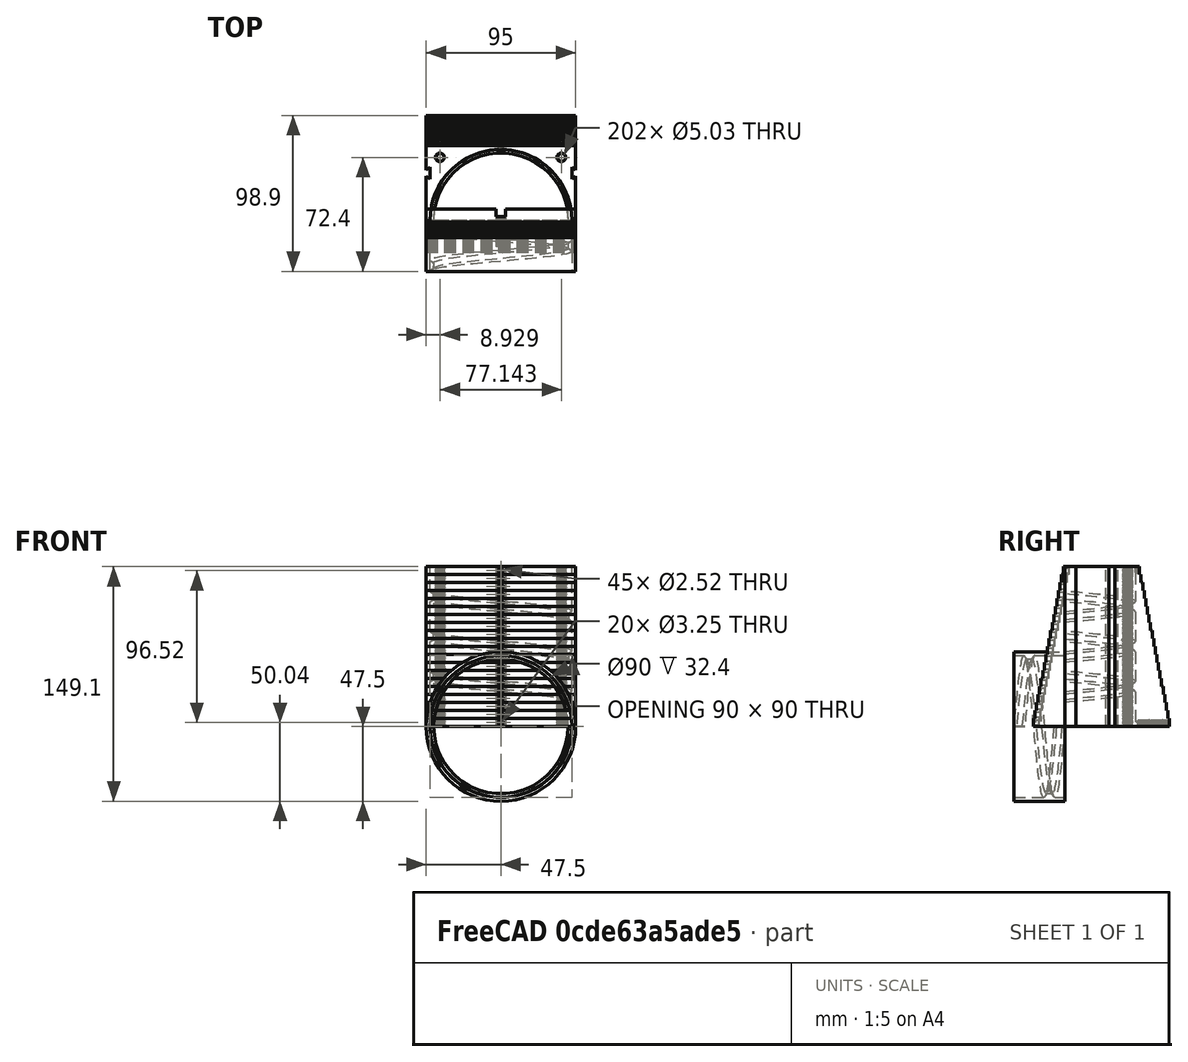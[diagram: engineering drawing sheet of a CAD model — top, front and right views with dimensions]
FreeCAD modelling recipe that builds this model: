
FCSTD DOCUMENT  (FreeCAD 2023.131R26244 +5365 (Git))
Label: Dewalt DW6184 Height Adjust
License: All rights reserved
LicenseURL: http://en.wikipedia.org/wiki/All_rights_reserved
objects: Sketcher::SketchObject×13, PartDesign::Pad×5, PartDesign::Pocket×3, PartDesign::Hole×3, PartDesign::Body×3, PartDesign::AdditiveHelix×2, Spreadsheet::Sheet×1, PartDesign::LinearPattern×1
note: 71 computed .brp shape members not serialized (recipe doc carries the construction recipe); baked Part::Feature solids carry a one-line shape summary decoded from their .brp

FEATURE [Spreadsheet::Sheet] Spreadsheet  label="Parameters"
  PythonMode = false
  ShowCells = 0
  TreeRank = 1
  cells = A1=Thickness; B1(thickness)=2.5; A2=Outer Diameter; B2(outer_diameter)=90; A3=Height; B3(height)==4"; A5=Thread Inner Width; B5(thread_small_width)=3.5; C5=4; A6=Thread Outer Width; B6(thread_large_width)=7; C6=7.5; A7=Thread Depth; B7(thread_depth)=2.3; C7=2.5; A8=Thread Turns; B8(thread_turns)=4; A9=Thread Pitch; B9(thread_pitch)==height / thread_turns; A11=Step Height Change; B11(step_height)=1; A13=Dovetail Inner Width; B13(dovetail_large_width)=7.5; A14=Dovetaile Outer Width; B14(dovetail_small_width)=4; A15=Dovetail Depth; B15(dovetail_depth)=2.5
FEATURE [Sketcher::SketchObject] Sketch
  ArcFitTolerance = 1e-06
  AttachmentSupport = -> [XY_Plane]
  ExternalBSplineMaxDegree = 5
  ExternalBSplineTolerance = 0.0001
  FullyConstrained = true
  InternalTolerance = 1e-06
  InvalidShape = false
  MakeInternals = false
  MapMode = 5
  Support = -> [XY_Plane]
  TreeRank = 12
  ValidateShape = true
  expr: Constraints[11] = <<Parameters>>.outer_diameter / 2 + <<Parameters>>.thickness - <<Parameters>>.step_height
  expr: Constraints[1] = <<Parameters>>.outer_diameter
  expr: Constraints[21] = <<Parameters>>.dovetail_small_width
  expr: Constraints[22] = <<Parameters>>.dovetail_large_width
  expr: Constraints[23] = <<Parameters>>.dovetail_depth
  expr: Constraints[26] = <<Parameters>>.outer_diameter / 3
  expr: Constraints[31] = <<Parameters>>.dovetail_large_width
  expr: Constraints[32] = <<Parameters>>.dovetail_small_width
  expr: Constraints[34] = <<Parameters>>.dovetail_depth
  expr: Constraints[36] = <<Parameters>>.outer_diameter / 3
  expr: Constraints[8] = <<Parameters>>.outer_diameter + 2 * <<Parameters>>.thickness
  sketch-geometry (16):
    g0: ArcOfCircle CenterX=0 CenterY=0 CenterZ=0 NormalX=0 NormalY=0 NormalZ=1 AngleXU=0 Radius=45 StartAngle=0 EndAngle=3.14159
    g1: LineSegment StartX=-47.5 StartY=0 StartZ=0 EndX=-45 EndY=0 EndZ=0
    g2: LineSegment StartX=47.5 StartY=0 StartZ=0 EndX=47.5 EndY=28 EndZ=0
    g3: LineSegment StartX=47.5 StartY=46.5 StartZ=0 EndX=-47.5 EndY=46.5 EndZ=0
    g4: LineSegment StartX=-47.5 StartY=46.5 StartZ=0 EndX=-47.5 EndY=32 EndZ=0
    g5: LineSegment StartX=45 StartY=0 StartZ=0 EndX=47.5 EndY=0 EndZ=0
    g6: LineSegment StartX=-47.5 StartY=32 StartZ=0 EndX=-45 EndY=33.75 EndZ=0
    g7: LineSegment StartX=-45 StartY=33.75 StartZ=0 EndX=-45 EndY=26.25 EndZ=0
    g8: LineSegment StartX=-45 StartY=26.25 StartZ=0 EndX=-47.5 EndY=28 EndZ=0
    g9: GeomPoint [constr] X=-45 Y=30 Z=0
    g10: LineSegment StartX=45 StartY=33.75 StartZ=0 EndX=45 EndY=26.25 EndZ=0
    g11: LineSegment StartX=45 StartY=26.25 StartZ=0 EndX=47.5 EndY=28 EndZ=0
    g12: LineSegment StartX=45 StartY=33.75 StartZ=0 EndX=47.5 EndY=32 EndZ=0
    g13: GeomPoint [constr] X=45 Y=30 Z=0
    g14: LineSegment StartX=-47.5 StartY=28 StartZ=0 EndX=-47.5 EndY=0 EndZ=0
    g15: LineSegment StartX=47.5 StartY=32 StartZ=0 EndX=47.5 EndY=46.5 EndZ=0
  constraints (45):
    c: Coincident(g0,g-1)
    c: Diameter(g0) = 90
    c: Coincident(g15,g3)
    c: Coincident(g3,g4)
    c: Coincident(g14,g1)
    c: Horizontal(g1)
    c: Horizontal(g3)
    c: Vertical(g4)
    c: DistanceX(g1,g5) = 95
    c: Symmetric(g1,g5,g0)
    c: Vertical(g2)
    c: DistanceY(g5,g15) = 46.5
    c: Coincident(g2,g5)
    c: Coincident(g1,g0)
    c: Coincident(g5,g0)
    c: PointOnObject(g0,g-1)
    c: PointOnObject(g0,g-1)
    c: Coincident(g7,g6)
    c: Vertical(g7)
    c: Coincident(g8,g7)
    c: Equal(g6,g8)
    c: DistanceY(g8,g6) = 4
    c: DistanceY(g7,g6) = 7.5
    c: DistanceX(g6,g6) = 2.5
    c: DistanceX(g8,g6) = 0
    c: Symmetric(g6,g7,g9)
    c: DistanceY(g0,g9) = 30
    c: Vertical(g10)
    c: Coincident(g11,g10)
    c: Coincident(g12,g10)
    c: Equal(g12,g11)
    c: DistanceY(g10,g10) = 7.5
    c: DistanceY(g11,g12) = 4
    c: DistanceX(g12,g11) = 0
    c: DistanceX(g10,g11) = 2.5
    c: Symmetric(g10,g10,g13)
    c: DistanceY(g0,g13) = 30
    c: Coincident(g4,g6)
    c: PointOnObject(g14,g8)
    c: PointOnObject(g2,g11)
    c: Coincident(g15,g12)
    c: Vertical(g14)
    c: DistanceX(g3,g1) = 0
    c: Vertical(g15)
    c: DistanceX(g3,g2) = 0
FEATURE [PartDesign::Pad] Pad
  AddSubType = 0
  AlongSketchNormal = false
  AutoTaperInnerAngle = true
  CheckUpToFaceLimits = true
  ClaimChildren = false
  Direction = (0,0,1)
  Fit = 0
  FitJoin = 0
  InnerFit = 0
  InnerFitJoin = 0
  InvalidShape = false
  Length = 101.6
  Length2 = 100
  Linearize = true
  NewSolid = false
  Profile = -> Sketch
  Suppress = false
  TaperInnerAngle = 0
  TaperInnerAngleRev = 0
  TreeRank = 13
  Type = 0
  ValidateShape = true
  _ProfileBasedVersion = 1
  expr: Length = <<Parameters>>.height
FEATURE [Sketcher::SketchObject] Sketch001
  ArcFitTolerance = 1e-06
  AttachmentSupport = -> [XZ_Plane]
  ExternalBSplineMaxDegree = 5
  ExternalBSplineTolerance = 0.0001
  FullyConstrained = true
  InternalTolerance = 1e-06
  InvalidShape = false
  MakeInternals = false
  MapMode = 5
  Placement = pos=(0,0,0) rot=(1,0,0;1.5708rad)
  Support = -> [XZ_Plane]
  TreeRank = 14
  ValidateShape = true
  expr: Constraints[10] = <<Parameters>>.outer_diameter / 2 + 0.1
  expr: Constraints[11] = <<Parameters>>.thread_large_width / 5 * 2
  expr: Constraints[7] = <<Parameters>>.thread_large_width
  expr: Constraints[8] = <<Parameters>>.thread_small_width
  expr: Constraints[9] = <<Parameters>>.thread_depth
  sketch-geometry (4):
    g0: LineSegment StartX=-45.1 StartY=9.8 StartZ=0 EndX=-45.1 EndY=2.8 EndZ=0
    g1: LineSegment StartX=-42.8 StartY=8.05 StartZ=0 EndX=-42.8 EndY=4.55 EndZ=0
    g2: LineSegment StartX=-45.1 StartY=9.8 StartZ=0 EndX=-42.8 EndY=8.05 EndZ=0
    g3: LineSegment StartX=-45.1 StartY=2.8 StartZ=0 EndX=-42.8 EndY=4.55 EndZ=0
  constraints (12):
    c: Vertical(g0)
    c: Vertical(g1)
    c: Coincident(g2,g0)
    c: Coincident(g2,g1)
    c: Coincident(g3,g0)
    c: Coincident(g3,g1)
    c: Equal(g2,g3)
    c: DistanceY(g0,g0) = 7
    c: DistanceY(g1,g1) = 3.5
    c: DistanceX(g0,g1) = 2.3
    c: DistanceX(g0,g-1) = 45.1
    c: DistanceY(g-1,g0) = 2.8
FEATURE [PartDesign::AdditiveHelix] Helix
  AddSubType = 0
  Angle = 0
  Axis = (0,-2e-16,1)
  Base = (0,0,0)
  BaseFeature = -> Pad
  ClaimChildren = false
  Fit = 0
  FitJoin = 0
  Growth = 0
  HasBeenEdited = true
  Height = 80
  InnerFit = 0
  InnerFitJoin = 0
  InvalidShape = false
  LeftHanded = false
  Linearize = true
  Mode = 0
  NewSolid = false
  Outside = false
  Pitch = 25.4
  Profile = -> Sketch001
  ReferenceAxis = -> Sketch001 [V_Axis]
  Suppress = false
  TreeRank = 15
  Turns = 3.14961
  ValidateShape = true
  _ProfileBasedVersion = 1
  expr: Pitch = <<Parameters>>.thread_pitch
  expr: Turns = <<Parameters>>.thread_turns
FEATURE [Sketcher::SketchObject] Sketch002
  ArcFitTolerance = 1e-06
  AttachmentSupport = -> [Helix]
  ExternalBSplineMaxDegree = 5
  ExternalBSplineTolerance = 0.0001
  FullyConstrained = false
  InternalTolerance = 1e-06
  InvalidShape = false
  MakeInternals = false
  MapMode = 5
  Placement = pos=(0,0,101.6) rot=(0,0,1;0rad)
  Support = -> [Helix]
  TreeRank = 16
  ValidateShape = true
  expr: Constraints[10] = <<Parameters>>.outer_diameter / 2 + 0.2
  expr: Constraints[9] = <<Parameters>>.outer_diameter + 2 * <<Parameters>>.thickness
  sketch-geometry (4):
    g0: LineSegment StartX=-47.4962 StartY=0 StartZ=0 EndX=47.5038 EndY=0 EndZ=0
    g1: LineSegment StartX=47.5038 StartY=0 StartZ=0 EndX=47.5038 EndY=-45.2 EndZ=0
    g2: LineSegment StartX=47.5038 StartY=-45.2 StartZ=0 EndX=-47.4962 EndY=-45.2 EndZ=0
    g3: LineSegment StartX=-47.4962 StartY=-45.2 StartZ=0 EndX=-47.4962 EndY=0 EndZ=0
  constraints (11):
    c: Coincident(g0,g1)
    c: Coincident(g1,g2)
    c: Coincident(g2,g3)
    c: Coincident(g3,g0)
    c: Horizontal(g0)
    c: Horizontal(g2)
    c: Vertical(g1)
    c: Vertical(g3)
    c: PointOnObject(g0,g-1)
    c: DistanceX(g0,g0) = 95
    c: DistanceY(g1,g0) = 45.2
FEATURE [PartDesign::Pocket] Pocket
  AddSubType = 1
  AutoTaperInnerAngle = true
  BaseFeature = -> Helix
  CheckUpToFaceLimits = true
  ClaimChildren = false
  Fit = 0
  FitJoin = 0
  InnerFit = 0
  InnerFitJoin = 0
  InvalidShape = false
  Length = 500
  Length2 = 500
  Linearize = true
  NewSolid = false
  Profile = -> Sketch002
  Suppress = false
  TaperInnerAngle = 0
  TaperInnerAngleRev = 0
  TreeRank = 17
  Type = 4
  ValidateShape = true
  _ProfileBasedVersion = 1
  _Version = 1
FEATURE [Sketcher::SketchObject] Sketch003
  ArcFitTolerance = 1e-06
  AttachmentSupport = -> [Pocket]
  ExternalBSplineMaxDegree = 5
  ExternalBSplineTolerance = 0.0001
  FullyConstrained = true
  InternalTolerance = 1e-06
  InvalidShape = false
  MakeInternals = false
  MapMode = 5
  Placement = pos=(-47.5,0,0) rot=(0.57735,-0.57735,-0.57735;2.0944rad)
  Support = -> [Pocket]
  TreeRank = 18
  ValidateShape = true
  expr: Constraints[2] = <<Parameters>>.outer_diameter / 2 + <<Parameters>>.thickness - <<Parameters>>.step_height
  expr: Constraints[3] = <<Parameters>>.height
  expr: Constraints[7] = <<Parameters>>.step_height
  sketch-geometry (42):
    g0: LineSegment StartX=-46.5 StartY=101.6 StartZ=0 EndX=-46.5 EndY=0 EndZ=0
    g1: LineSegment StartX=-47.5 StartY=101.6 StartZ=0 EndX=-47.5 EndY=96.52 EndZ=0
    g2: LineSegment StartX=-48.5 StartY=96.52 StartZ=0 EndX=-48.5 EndY=91.44 EndZ=0
    g3: LineSegment StartX=-47.5 StartY=96.52 StartZ=0 EndX=-48.5 EndY=96.52 EndZ=0
    g4: LineSegment StartX=-48.5 StartY=91.44 StartZ=0 EndX=-49.5 EndY=91.44 EndZ=0
    g5: LineSegment StartX=-49.5 StartY=91.44 StartZ=0 EndX=-49.5 EndY=86.36 EndZ=0
    g6: LineSegment StartX=-49.5 StartY=86.36 StartZ=0 EndX=-50.5 EndY=86.36 EndZ=0
    g7: LineSegment StartX=-50.5 StartY=86.36 StartZ=0 EndX=-50.5 EndY=81.28 EndZ=0
    g8: LineSegment StartX=-50.5 StartY=81.28 StartZ=0 EndX=-51.5 EndY=81.28 EndZ=0
    g9: LineSegment StartX=-51.5 StartY=81.28 StartZ=0 EndX=-51.5 EndY=76.2 EndZ=0
    g10: LineSegment StartX=-51.5 StartY=76.2 StartZ=0 EndX=-52.5 EndY=76.2 EndZ=0
    g11: LineSegment StartX=-52.5 StartY=76.2 StartZ=0 EndX=-52.5 EndY=71.12 EndZ=0
    g12: LineSegment StartX=-47.5 StartY=101.6 StartZ=0 EndX=-46.5 EndY=101.6 EndZ=0
    g13: LineSegment StartX=-52.5 StartY=71.12 StartZ=0 EndX=-53.5 EndY=71.12 EndZ=0
    g14: LineSegment StartX=-53.5 StartY=71.12 StartZ=0 EndX=-53.5 EndY=66.04 EndZ=0
    g15: LineSegment StartX=-53.5 StartY=66.04 StartZ=0 EndX=-54.5 EndY=66.04 EndZ=0
    g16: LineSegment StartX=-54.5 StartY=66.04 StartZ=0 EndX=-54.5 EndY=60.96 EndZ=0
    g17: LineSegment StartX=-54.5 StartY=60.96 StartZ=0 EndX=-55.5 EndY=60.96 EndZ=0
    g18: LineSegment StartX=-55.5 StartY=60.96 StartZ=0 EndX=-55.5 EndY=55.88 EndZ=0
    g19: LineSegment StartX=-55.5 StartY=55.88 StartZ=0 EndX=-56.5 EndY=55.88 EndZ=0
    g20: LineSegment StartX=-56.5 StartY=55.88 StartZ=0 EndX=-56.5 EndY=50.8 EndZ=0
    g21: LineSegment StartX=-56.5 StartY=50.8 StartZ=0 EndX=-57.5 EndY=50.8 EndZ=0
    g22: LineSegment StartX=-57.5 StartY=50.8 StartZ=0 EndX=-57.5 EndY=45.72 EndZ=0
    g23: LineSegment StartX=-57.5 StartY=45.72 StartZ=0 EndX=-58.5 EndY=45.72 EndZ=0
    g24: LineSegment StartX=-58.5 StartY=45.72 StartZ=0 EndX=-58.5 EndY=40.64 EndZ=0
    g25: LineSegment StartX=-58.5 StartY=40.64 StartZ=0 EndX=-59.5 EndY=40.64 EndZ=0
    g26: LineSegment StartX=-59.5 StartY=40.64 StartZ=0 EndX=-59.5 EndY=35.56 EndZ=0
    g27: LineSegment StartX=-59.5 StartY=35.56 StartZ=0 EndX=-60.5 EndY=35.56 EndZ=0
    g28: LineSegment StartX=-60.5 StartY=35.56 StartZ=0 EndX=-60.5 EndY=30.48 EndZ=0
    g29: LineSegment StartX=-60.5 StartY=30.48 StartZ=0 EndX=-61.5 EndY=30.48 EndZ=0
    g30: LineSegment StartX=-61.5 StartY=30.48 StartZ=0 EndX=-61.5 EndY=25.4 EndZ=0
    g31: LineSegment StartX=-61.5 StartY=25.4 StartZ=0 EndX=-62.5 EndY=25.4 EndZ=0
    g32: LineSegment StartX=-62.5 StartY=25.4 StartZ=0 EndX=-62.5 EndY=20.32 EndZ=0
    g33: LineSegment StartX=-62.5 StartY=20.32 StartZ=0 EndX=-63.5 EndY=20.32 EndZ=0
    g34: LineSegment StartX=-63.5 StartY=20.32 StartZ=0 EndX=-63.5 EndY=15.24 EndZ=0
    g35: LineSegment StartX=-63.5 StartY=15.24 StartZ=0 EndX=-64.5 EndY=15.24 EndZ=0
    g36: LineSegment StartX=-64.5 StartY=15.24 StartZ=0 EndX=-64.5 EndY=10.16 EndZ=0
    g37: LineSegment StartX=-64.5 StartY=10.16 StartZ=0 EndX=-65.5 EndY=10.16 EndZ=0
    g38: LineSegment StartX=-65.5 StartY=10.16 StartZ=0 EndX=-65.5 EndY=5.08 EndZ=0
    g39: LineSegment StartX=-65.5 StartY=5.08 StartZ=0 EndX=-66.5 EndY=5.08 EndZ=0
    g40: LineSegment StartX=-66.5 StartY=5.08 StartZ=0 EndX=-66.5 EndY=0 EndZ=0
    g41: LineSegment StartX=-66.5 StartY=0 StartZ=0 EndX=-46.5 EndY=0 EndZ=0
  constraints (126):
    c: PointOnObject(g0,g-1)
    c: Vertical(g0)
    c: DistanceX(g0,g-1) = 46.5
    c: DistanceY(g0,g0) = 101.6
    c: Vertical(g1)
    c: Vertical(g2)
    c: Equal(g1,g2)
    c: DistanceX(g2,g1) = 1
    c: Coincident(g3,g1)
    c: Horizontal(g3)
    c: Coincident(g2,g3)
    c: Coincident(g4,g2)
    c: Horizontal(g4)
    c: Coincident(g5,g4)
    c: Vertical(g5)
    c: Equal(g3,g4)
    c: Coincident(g6,g5)
    c: Horizontal(g6)
    c: Coincident(g7,g6)
    c: Vertical(g7)
    c: Coincident(g8,g7)
    c: Horizontal(g8)
    c: Coincident(g9,g8)
    c: Vertical(g9)
    c: Coincident(g10,g9)
    c: Horizontal(g10)
    c: Coincident(g11,g10)
    c: Vertical(g11)
    c: Equal(g3,g6)
    c: Equal(g3,g8)
    c: Equal(g3,g10)
    c: Equal(g1,g5)
    c: Equal(g1,g7)
    c: Equal(g1,g9)
    c: Equal(g1,g11)
    c: Coincident(g12,g1)
    c: Horizontal(g12)
    c: Equal(g3,g12)
    c: Coincident(g12,g0)
    c: Coincident(g13,g11)
    c: Horizontal(g13)
    c: Coincident(g14,g13)
    c: Vertical(g14)
    c: Coincident(g15,g14)
    c: Horizontal(g15)
    c: Coincident(g16,g15)
    c: Vertical(g16)
    c: Coincident(g17,g16)
    c: Horizontal(g17)
    c: Coincident(g18,g17)
    c: Vertical(g18)
    c: Coincident(g19,g18)
    c: Horizontal(g19)
    c: Coincident(g20,g19)
    c: Vertical(g20)
    c: Coincident(g21,g20)
    c: Horizontal(g21)
    c: Coincident(g22,g21)
    c: Vertical(g22)
    c: Coincident(g23,g22)
    c: Horizontal(g23)
    c: Coincident(g24,g23)
    c: Vertical(g24)
    c: Coincident(g25,g24)
    c: Horizontal(g25)
    c: Coincident(g26,g25)
    c: Vertical(g26)
    c: Coincident(g27,g26)
    c: Horizontal(g27)
    c: Coincident(g28,g27)
    c: Vertical(g28)
    c: Coincident(g29,g28)
    c: Horizontal(g29)
    c: Coincident(g30,g29)
    c: Vertical(g30)
    c: Coincident(g31,g30)
    c: Horizontal(g31)
    c: Coincident(g32,g31)
    c: Vertical(g32)
    c: Coincident(g33,g32)
    c: Horizontal(g33)
    c: Coincident(g34,g33)
    c: Vertical(g34)
    c: Coincident(g35,g34)
    c: Horizontal(g35)
    c: Coincident(g36,g35)
    c: Vertical(g36)
    c: Coincident(g37,g36)
    c: Horizontal(g37)
    c: Coincident(g38,g37)
    c: Vertical(g38)
    c: Coincident(g39,g38)
    c: Horizontal(g39)
    c: Coincident(g40,g39)
    c: Vertical(g40)
    c: Equal(g13,g10)
    c: Equal(g13,g15)
    c: Equal(g15,g17)
    c: Equal(g17,g19)
    c: Equal(g19,g21)
    c: Equal(g21,g23)
    c: Equal(g23,g25)
    c: Equal(g25,g27)
    c: Equal(g27,g29)
    c: Equal(g29,g31)
    c: Equal(g31,g33)
    c: Equal(g33,g35)
    c: Equal(g35,g37)
    c: Equal(g37,g39)
    c: Equal(g11,g14)
    c: Equal(g14,g16)
    c: Equal(g16,g18)
    c: Equal(g18,g20)
    c: Equal(g20,g22)
    c: Equal(g22,g24)
    c: Equal(g24,g26)
    c: Equal(g26,g28)
    c: Equal(g28,g30)
    c: Equal(g30,g32)
    c: Equal(g32,g34)
    c: Equal(g34,g36)
    c: Equal(g36,g38)
    c: Equal(g38,g40)
    c: PointOnObject(g40,g-1)
    c: Coincident(g41,g40)
    c: Coincident(g41,g0)
FEATURE [PartDesign::Pad] Pad001
  AddSubType = 0
  AlongSketchNormal = false
  AutoTaperInnerAngle = true
  BaseFeature = -> Pocket
  CheckUpToFaceLimits = true
  ClaimChildren = false
  Direction = (-1,0,0)
  Fit = 0
  FitJoin = 0
  InnerFit = 0
  InnerFitJoin = 0
  InvalidShape = false
  Length = 95
  Length2 = 100
  Linearize = true
  NewSolid = false
  Profile = -> Sketch003
  Reversed = true
  Suppress = false
  TaperInnerAngle = 0
  TaperInnerAngleRev = 0
  TreeRank = 19
  Type = 0
  ValidateShape = true
  _ProfileBasedVersion = 1
  expr: Length = <<Parameters>>.outer_diameter + 2 * <<Parameters>>.thickness
FEATURE [Sketcher::SketchObject] Sketch004
  ArcFitTolerance = 1e-06
  AttachmentSupport = -> [Pad001]
  ExternalBSplineMaxDegree = 5
  ExternalBSplineTolerance = 0.0001
  FullyConstrained = true
  InternalTolerance = 1e-06
  InvalidShape = false
  MakeInternals = false
  MapMode = 5
  Placement = pos=(0,0,101.6) rot=(0,0,1;0rad)
  Support = -> [Pad001]
  TreeRank = 20
  ValidateShape = true
  expr: Constraints[1] = <<Parameters>>.outer_diameter / 9 * 4
  expr: Constraints[2] = <<Parameters>>.outer_diameter / 7 * 6
  sketch-geometry (2):
    g0: Circle CenterX=-38.5714 CenterY=40 CenterZ=0 NormalX=0 NormalY=0 NormalZ=1 AngleXU=0 Radius=3
    g1: Circle CenterX=38.5714 CenterY=40 CenterZ=0 NormalX=0 NormalY=0 NormalZ=1 AngleXU=0 Radius=3
  constraints (5):
    c: Symmetric(g0,g1,g-2)
    c: DistanceY(g-1,g0) = 40
    c: DistanceX(g0,g1) = 77.1429
    c: Equal(g0,g1)
    c: Diameter(g0) = 6
FEATURE [PartDesign::Hole] Hole
  AddSubType = 1
  BaseFeature = -> Pad001
  ClaimChildren = false
  CustomThreadClearance = 0
  Depth = 101.6
  DepthType = 0
  Diameter = 5.026
  DrillForDepth = false
  DrillPoint = 0
  DrillPointAngle = 118
  Fit = 0
  FitJoin = 0
  HoleCutCountersinkAngle = 90
  HoleCutCustomValues = false
  HoleCutDepth = 0
  HoleCutDiameter = 6.1
  HoleCutType = 0
  InnerFit = 0
  InnerFitJoin = 0
  InvalidShape = false
  Linearize = true
  ModelThread = true
  NewSolid = false
  Profile = -> Sketch004
  Suppress = false
  Tapered = false
  TaperedAngle = 90
  ThreadClass = 0
  ThreadDepth = 101.6
  ThreadDepthType = 0
  ThreadDirection = 0
  ThreadFit = 0
  ThreadSize = 14
  ThreadType = 1
  Threaded = true
  TreeRank = 21
  UseCustomThreadClearance = false
  ValidateShape = true
  _ProfileBasedVersion = 1
  expr: Depth = <<Parameters>>.height
FEATURE [Sketcher::SketchObject] Sketch005
  ArcFitTolerance = 1e-06
  AttachmentSupport = -> [Hole]
  ExternalBSplineMaxDegree = 5
  ExternalBSplineTolerance = 0.0001
  FullyConstrained = true
  InternalTolerance = 1e-06
  InvalidShape = false
  MakeInternals = false
  MapMode = 5
  Placement = pos=(0,66.5,0) rot=(0,0.707107,0.707107;3.14159rad)
  Support = -> [Hole]
  TreeRank = 22
  ValidateShape = true
  expr: Constraints[2] = <<Parameters>>.height / 20 / 2
  sketch-geometry (1):
    g0: Circle CenterX=0 CenterY=2.54 CenterZ=0 NormalX=0 NormalY=0 NormalZ=1 AngleXU=0 Radius=1.5
  constraints (3):
    c: PointOnObject(g0,g-2)
    c: Diameter(g0) = 3
    c: DistanceY(g-1,g0) = 2.54
FEATURE [PartDesign::Hole] Hole001
  AddSubType = 1
  BaseFeature = -> Hole
  ClaimChildren = false
  CustomThreadClearance = 0
  Depth = 20
  DepthType = 0
  Diameter = 2.52
  DrillForDepth = false
  DrillPoint = 1
  DrillPointAngle = 118
  Fit = 0
  FitJoin = 0
  HoleCutCountersinkAngle = 90
  HoleCutCustomValues = false
  HoleCutDepth = 0
  HoleCutDiameter = 6.1
  HoleCutType = 0
  InnerFit = 0
  InnerFitJoin = 0
  InvalidShape = false
  Linearize = true
  ModelThread = true
  NewSolid = false
  Profile = -> Sketch005
  Suppress = false
  Tapered = false
  TaperedAngle = 90
  ThreadClass = 0
  ThreadDepth = 20
  ThreadDepthType = 0
  ThreadDirection = 0
  ThreadFit = 0
  ThreadSize = 9
  ThreadType = 1
  Threaded = true
  TreeRank = 23
  UseCustomThreadClearance = false
  ValidateShape = true
  _ProfileBasedVersion = 1
  expr: Depth = 20
FEATURE [Sketcher::SketchObject] Sketch006
  ArcFitTolerance = 1e-06
  AttachmentSupport = -> [Hole001]
  ExternalBSplineMaxDegree = 5
  ExternalBSplineTolerance = 0.0001
  FullyConstrained = false
  InternalTolerance = 1e-06
  InvalidShape = false
  MakeInternals = false
  MapMode = 5
  Placement = pos=(0,47.5,0) rot=(0,0.707107,0.707107;3.14159rad)
  Support = -> [Hole001]
  TreeRank = 24
  ValidateShape = true
  expr: Constraints[1] = <<Parameters>>.height / 40 * 39
  sketch-geometry (1):
    g0: Circle CenterX=0 CenterY=99.06 CenterZ=0 NormalX=0 NormalY=0 NormalZ=1 AngleXU=0 Radius=2.09662
  constraints (2):
    c: PointOnObject(g0,g-2)
    c: DistanceY(g-1,g0) = 99.06
FEATURE [PartDesign::Hole] Hole002
  AddSubType = 1
  BaseFeature = -> Hole001
  ClaimChildren = false
  CustomThreadClearance = 0
  Depth = 5
  DepthType = 0
  Diameter = 2.52
  DrillForDepth = false
  DrillPoint = 1
  DrillPointAngle = 118
  Fit = 0
  FitJoin = 0
  HoleCutCountersinkAngle = 90
  HoleCutCustomValues = false
  HoleCutDepth = 0
  HoleCutDiameter = 6.1
  HoleCutType = 0
  InnerFit = 0
  InnerFitJoin = 0
  InvalidShape = false
  Linearize = true
  ModelThread = true
  NewSolid = false
  Profile = -> Sketch006
  Suppress = false
  Tapered = false
  TaperedAngle = 90
  ThreadClass = 0
  ThreadDepth = 5
  ThreadDepthType = 0
  ThreadDirection = 0
  ThreadFit = 0
  ThreadSize = 9
  ThreadType = 1
  Threaded = true
  TreeRank = 25
  UseCustomThreadClearance = false
  ValidateShape = true
  _ProfileBasedVersion = 1
FEATURE [PartDesign::Body] Body  label="Cradle"
  AutoGroupSolids = false
  ClaimAllChildren = false
  ExportMode = 0
  Group = -> [Sketch,Pad,Sketch001,Helix,Sketch002,Pocket,Sketch003,Pad001,Sketch004,Hole,Sketch005,Hole001,Sketch006,Hole002]
  InvalidShape = false
  Origin = -> Origin
  Tip = -> Hole002
  TreeRank = 11
  ValidateShape = true
  _ExportChildren = -> [Pad,Helix,Pocket,Pad001,Hole,Hole001,Hole002]
  _GroupVersion = 1
FEATURE [Sketcher::SketchObject] Sketch007
  ArcFitTolerance = 1e-06
  AttachmentOffset = pos=(0,0,-47.5) rot=(0,0,1;0rad)
  AttachmentSupport = -> [YZ_Plane001]
  ExternalBSplineMaxDegree = 5
  ExternalBSplineTolerance = 0.0001
  FullyConstrained = true
  InternalTolerance = 1e-06
  InvalidShape = false
  MakeInternals = false
  MapMode = 5
  Placement = pos=(-47.5,1.05e-14,-1.05e-14) rot=(0.57735,0.57735,0.57735;2.0944rad)
  Support = -> [YZ_Plane001]
  TreeRank = 36
  ValidateShape = true
  expr: AttachmentOffset.Base.z = -<<Parameters>>.outer_diameter / 2 - <<Parameters>>.thickness
  expr: Constraints[124] = <<Parameters>>.step_height
  expr: Constraints[2] = <<Parameters>>.height
  sketch-geometry (42):
    g0: LineSegment StartX=0 StartY=0 StartZ=0 EndX=0 EndY=101.6 EndZ=0
    g1: LineSegment StartX=0 StartY=101.6 StartZ=0 EndX=-1 EndY=101.6 EndZ=0
    g2: LineSegment StartX=-1 StartY=101.6 StartZ=0 EndX=-1 EndY=96.52 EndZ=0
    g3: LineSegment StartX=-1 StartY=96.52 StartZ=0 EndX=-2 EndY=96.52 EndZ=0
    g4: LineSegment StartX=-2 StartY=96.52 StartZ=0 EndX=-2 EndY=91.44 EndZ=0
    g5: LineSegment StartX=-2 StartY=91.44 StartZ=0 EndX=-3 EndY=91.44 EndZ=0
    g6: LineSegment StartX=-3 StartY=91.44 StartZ=0 EndX=-3 EndY=86.36 EndZ=0
    g7: LineSegment StartX=-3 StartY=86.36 StartZ=0 EndX=-4 EndY=86.36 EndZ=0
    g8: LineSegment StartX=-4 StartY=86.36 StartZ=0 EndX=-4 EndY=81.28 EndZ=0
    g9: LineSegment StartX=-4 StartY=81.28 StartZ=0 EndX=-5 EndY=81.28 EndZ=0
    g10: LineSegment StartX=-5 StartY=81.28 StartZ=0 EndX=-5 EndY=76.2 EndZ=0
    g11: LineSegment StartX=-5 StartY=76.2 StartZ=0 EndX=-6 EndY=76.2 EndZ=0
    g12: LineSegment StartX=-6 StartY=76.2 StartZ=0 EndX=-6 EndY=71.12 EndZ=0
    g13: LineSegment StartX=-6 StartY=71.12 StartZ=0 EndX=-7 EndY=71.12 EndZ=0
    g14: LineSegment StartX=-7 StartY=71.12 StartZ=0 EndX=-7 EndY=66.04 EndZ=0
    g15: LineSegment StartX=-7 StartY=66.04 StartZ=0 EndX=-8 EndY=66.04 EndZ=0
    g16: LineSegment StartX=-8 StartY=66.04 StartZ=0 EndX=-8 EndY=60.96 EndZ=0
    g17: LineSegment StartX=-8 StartY=60.96 StartZ=0 EndX=-9 EndY=60.96 EndZ=0
    g18: LineSegment StartX=-9 StartY=60.96 StartZ=0 EndX=-9 EndY=55.88 EndZ=0
    g19: LineSegment StartX=-9 StartY=55.88 StartZ=0 EndX=-10 EndY=55.88 EndZ=0
    g20: LineSegment StartX=-10 StartY=55.88 StartZ=0 EndX=-10 EndY=50.8 EndZ=0
    g21: LineSegment StartX=-10 StartY=50.8 StartZ=0 EndX=-11 EndY=50.8 EndZ=0
    g22: LineSegment StartX=-11 StartY=50.8 StartZ=0 EndX=-11 EndY=45.72 EndZ=0
    g23: LineSegment StartX=-11 StartY=45.72 StartZ=0 EndX=-12 EndY=45.72 EndZ=0
    g24: LineSegment StartX=-12 StartY=45.72 StartZ=0 EndX=-12 EndY=40.64 EndZ=0
    g25: LineSegment StartX=-12 StartY=40.64 StartZ=0 EndX=-13 EndY=40.64 EndZ=0
    g26: LineSegment StartX=-13 StartY=40.64 StartZ=0 EndX=-13 EndY=35.56 EndZ=0
    g27: LineSegment StartX=-13 StartY=35.56 StartZ=0 EndX=-14 EndY=35.56 EndZ=0
    g28: LineSegment StartX=-14 StartY=35.56 StartZ=0 EndX=-14 EndY=30.48 EndZ=0
    g29: LineSegment StartX=-14 StartY=30.48 StartZ=0 EndX=-15 EndY=30.48 EndZ=0
    g30: LineSegment StartX=-15 StartY=30.48 StartZ=0 EndX=-15 EndY=25.4 EndZ=0
    g31: LineSegment StartX=-15 StartY=25.4 StartZ=0 EndX=-16 EndY=25.4 EndZ=0
    g32: LineSegment StartX=-16 StartY=25.4 StartZ=0 EndX=-16 EndY=20.32 EndZ=0
    g33: LineSegment StartX=-16 StartY=20.32 StartZ=0 EndX=-17 EndY=20.32 EndZ=0
    g34: LineSegment StartX=-17 StartY=20.32 StartZ=0 EndX=-17 EndY=15.24 EndZ=0
    g35: LineSegment StartX=-17 StartY=15.24 StartZ=0 EndX=-18 EndY=15.24 EndZ=0
    g36: LineSegment StartX=-18 StartY=15.24 StartZ=0 EndX=-18 EndY=10.16 EndZ=0
    g37: LineSegment StartX=-18 StartY=10.16 StartZ=0 EndX=-19 EndY=10.16 EndZ=0
    g38: LineSegment StartX=-19 StartY=10.16 StartZ=0 EndX=-19 EndY=5.08 EndZ=0
    g39: LineSegment StartX=-19 StartY=5.08 StartZ=0 EndX=-20 EndY=5.08 EndZ=0
    g40: LineSegment StartX=-20 StartY=5.08 StartZ=0 EndX=-20 EndY=0 EndZ=0
    g41: LineSegment StartX=-20 StartY=0 StartZ=0 EndX=0 EndY=0 EndZ=0
  constraints (125):
    c: Coincident(g0,g-1)
    c: PointOnObject(g0,g-2)
    c: DistanceY(g0,g0) = 101.6
    c: Coincident(g1,g0)
    c: Horizontal(g1)
    c: Coincident(g2,g1)
    c: Vertical(g2)
    c: Coincident(g3,g2)
    c: Horizontal(g3)
    c: Coincident(g4,g3)
    c: Vertical(g4)
    c: Coincident(g5,g4)
    c: Horizontal(g5)
    c: Coincident(g6,g5)
    c: Vertical(g6)
    c: Coincident(g7,g6)
    c: Horizontal(g7)
    c: Coincident(g8,g7)
    c: Vertical(g8)
    c: Coincident(g9,g8)
    c: Horizontal(g9)
    c: Coincident(g10,g9)
    c: Vertical(g10)
    c: Coincident(g11,g10)
    c: Coincident(g12,g11)
    c: Vertical(g12)
    c: Coincident(g13,g12)
    c: Coincident(g14,g13)
    c: Vertical(g14)
    c: Horizontal(g11)
    c: Horizontal(g13)
    c: Equal(g1,g3)
    c: Equal(g3,g5)
    c: Equal(g5,g7)
    c: Equal(g7,g9)
    c: Equal(g9,g11)
    c: Equal(g11,g13)
    c: Equal(g2,g4)
    c: Equal(g4,g6)
    c: Equal(g6,g8)
    c: Equal(g8,g10)
    c: Equal(g10,g12)
    c: Equal(g12,g14)
    c: Coincident(g15,g14)
    c: Horizontal(g15)
    c: Coincident(g16,g15)
    c: Vertical(g16)
    c: Coincident(g17,g16)
    c: Horizontal(g17)
    c: Coincident(g18,g17)
    c: Vertical(g18)
    c: Coincident(g19,g18)
    c: Horizontal(g19)
    c: Coincident(g20,g19)
    c: Vertical(g20)
    c: Coincident(g21,g20)
    c: Horizontal(g21)
    c: Coincident(g22,g21)
    c: Vertical(g22)
    c: Coincident(g23,g22)
    c: Horizontal(g23)
    c: Coincident(g24,g23)
    c: Vertical(g24)
    c: Coincident(g25,g24)
    c: Horizontal(g25)
    c: Coincident(g26,g25)
    c: Vertical(g26)
    c: Coincident(g27,g26)
    c: Horizontal(g27)
    c: Coincident(g28,g27)
    c: Vertical(g28)
    c: Coincident(g29,g28)
    c: Horizontal(g29)
    c: Coincident(g30,g29)
    c: Vertical(g30)
    c: Coincident(g31,g30)
    c: Horizontal(g31)
    c: Coincident(g32,g31)
    c: Vertical(g32)
    c: Coincident(g33,g32)
    c: Horizontal(g33)
    c: Coincident(g34,g33)
    c: Vertical(g34)
    c: Coincident(g35,g34)
    c: Horizontal(g35)
    c: Coincident(g36,g35)
    c: Vertical(g36)
    c: Coincident(g37,g36)
    c: Horizontal(g37)
    c: Coincident(g38,g37)
    c: Vertical(g38)
    c: Coincident(g39,g38)
    c: Horizontal(g39)
    c: Coincident(g40,g39)
    c: Vertical(g40)
    c: Coincident(g41,g40)
    c: Horizontal(g41)
    c: Equal(g13,g15)
    c: Equal(g15,g17)
    c: Equal(g17,g19)
    c: Equal(g19,g21)
    c: Equal(g21,g23)
    c: Equal(g23,g25)
    c: Equal(g25,g27)
    c: Equal(g27,g29)
    c: Equal(g29,g31)
    c: Equal(g31,g33)
    c: Equal(g33,g35)
    c: Equal(g35,g37)
    c: Equal(g37,g39)
    c: Equal(g14,g16)
    c: Equal(g16,g18)
    c: Equal(g18,g20)
    c: Equal(g20,g22)
    c: Equal(g22,g24)
    c: Equal(g24,g26)
    c: Equal(g26,g28)
    c: Equal(g28,g30)
    c: Equal(g30,g32)
    c: Equal(g32,g34)
    c: Equal(g34,g36)
    c: Equal(g36,g38)
    c: Equal(g38,g40)
    c: Coincident(g41,g0)
    c: DistanceX(g3,g2) = 1
FEATURE [PartDesign::Pad] Pad002
  AddSubType = 0
  AlongSketchNormal = false
  AutoTaperInnerAngle = true
  CheckUpToFaceLimits = true
  ClaimChildren = false
  Direction = (1,-2e-16,3e-16)
  Fit = 0
  FitJoin = 0
  InnerFit = 0
  InnerFitJoin = 0
  InvalidShape = false
  Length = 95
  Length2 = 100
  Linearize = true
  NewSolid = false
  Profile = -> Sketch007
  Suppress = false
  TaperInnerAngle = 0
  TaperInnerAngleRev = 0
  TreeRank = 37
  Type = 0
  ValidateShape = true
  _ProfileBasedVersion = 1
  expr: Length = <<Parameters>>.outer_diameter + 2 * <<Parameters>>.thickness
FEATURE [Sketcher::SketchObject] Sketch008
  ArcFitTolerance = 1e-06
  AttachmentSupport = -> [Pad002]
  ExternalBSplineMaxDegree = 5
  ExternalBSplineTolerance = 0.0001
  FullyConstrained = true
  InternalTolerance = 1e-06
  InvalidShape = false
  MakeInternals = false
  MapMode = 5
  Placement = pos=(0,0,0) rot=(0,0.707107,0.707107;3.14159rad)
  Support = -> [Pad002]
  TreeRank = 38
  ValidateShape = true
  expr: Constraints[10] = <<Parameters>>.height
  expr: Constraints[9] = <<Parameters>>.outer_diameter + 2 * <<Parameters>>.thickness
  sketch-geometry (4):
    g0: LineSegment StartX=-47.5 StartY=0 StartZ=0 EndX=47.5 EndY=0 EndZ=0
    g1: LineSegment StartX=47.5 StartY=0 StartZ=0 EndX=47.5 EndY=101.6 EndZ=0
    g2: LineSegment StartX=47.5 StartY=101.6 StartZ=0 EndX=-47.5 EndY=101.6 EndZ=0
    g3: LineSegment StartX=-47.5 StartY=101.6 StartZ=0 EndX=-47.5 EndY=0 EndZ=0
  constraints (11):
    c: Coincident(g0,g1)
    c: Coincident(g1,g2)
    c: Coincident(g2,g3)
    c: Coincident(g3,g0)
    c: Horizontal(g0)
    c: Horizontal(g2)
    c: Vertical(g1)
    c: Vertical(g3)
    c: Symmetric(g0,g0,g-1)
    c: DistanceX(g0,g0) = 95
    c: DistanceY(g0,g1) = 101.6
FEATURE [PartDesign::Pad] Pad003
  AddSubType = 0
  AlongSketchNormal = false
  AutoTaperInnerAngle = true
  BaseFeature = -> Pad002
  CheckUpToFaceLimits = true
  ClaimChildren = false
  Direction = (2e-16,1,-2e-16)
  Fit = 0
  FitJoin = 0
  InnerFit = 0
  InnerFitJoin = 0
  InvalidShape = false
  Length = 7
  Length2 = 100
  Linearize = true
  NewSolid = false
  Profile = -> Sketch008
  Suppress = false
  TaperInnerAngle = 0
  TaperInnerAngleRev = 0
  TreeRank = 39
  Type = 0
  ValidateShape = true
  _ProfileBasedVersion = 1
  expr: Length = <<Parameters>>.thickness + 4.5
FEATURE [Sketcher::SketchObject] Sketch009
  ArcFitTolerance = 1e-06
  AttachmentSupport = -> [YZ_Plane001]
  ExternalBSplineMaxDegree = 5
  ExternalBSplineTolerance = 0.0001
  FullyConstrained = true
  InternalTolerance = 1e-06
  InvalidShape = false
  MakeInternals = false
  MapMode = 5
  Placement = pos=(0,0,0) rot=(0.57735,0.57735,0.57735;2.0944rad)
  Support = -> [YZ_Plane001]
  TreeRank = 40
  ValidateShape = true
  expr: Constraints[124] = <<Parameters>>.thickness + 4.5
  expr: Constraints[125] = <<Parameters>>.thickness
  expr: Constraints[3] = <<Parameters>>.step_height
  expr: Constraints[40] = <<Parameters>>.height
  sketch-geometry (42):
    g0: LineSegment StartX=2.5 StartY=101.6 StartZ=0 EndX=2.5 EndY=96.52 EndZ=0
    g1: LineSegment StartX=2.5 StartY=96.52 StartZ=0 EndX=1.5 EndY=96.52 EndZ=0
    g2: LineSegment StartX=1.5 StartY=96.52 StartZ=0 EndX=1.5 EndY=91.44 EndZ=0
    g3: LineSegment StartX=1.5 StartY=91.44 StartZ=0 EndX=0.5 EndY=91.44 EndZ=0
    g4: LineSegment StartX=0.5 StartY=91.44 StartZ=0 EndX=0.5 EndY=86.36 EndZ=0
    g5: LineSegment StartX=0.5 StartY=86.36 StartZ=0 EndX=-0.5 EndY=86.36 EndZ=0
    g6: LineSegment StartX=-0.5 StartY=86.36 StartZ=0 EndX=-0.5 EndY=81.28 EndZ=0
    g7: LineSegment StartX=-0.5 StartY=81.28 StartZ=0 EndX=-1.5 EndY=81.28 EndZ=0
    g8: LineSegment StartX=-1.5 StartY=81.28 StartZ=0 EndX=-1.5 EndY=76.2 EndZ=0
    g9: LineSegment StartX=-1.5 StartY=76.2 StartZ=0 EndX=-2.5 EndY=76.2 EndZ=0
    g10: LineSegment StartX=-2.5 StartY=76.2 StartZ=0 EndX=-2.5 EndY=71.12 EndZ=0
    g11: LineSegment StartX=-2.5 StartY=71.12 StartZ=0 EndX=-3.5 EndY=71.12 EndZ=0
    g12: LineSegment StartX=-3.5 StartY=71.12 StartZ=0 EndX=-3.5 EndY=66.04 EndZ=0
    g13: LineSegment StartX=-3.5 StartY=66.04 StartZ=0 EndX=-4.5 EndY=66.04 EndZ=0
    g14: LineSegment StartX=-4.5 StartY=66.04 StartZ=0 EndX=-4.5 EndY=60.96 EndZ=0
    g15: LineSegment StartX=-4.5 StartY=60.96 StartZ=0 EndX=-5.5 EndY=60.96 EndZ=0
    g16: LineSegment StartX=-5.5 StartY=60.96 StartZ=0 EndX=-5.5 EndY=55.88 EndZ=0
    g17: LineSegment StartX=-5.5 StartY=55.88 StartZ=0 EndX=-6.5 EndY=55.88 EndZ=0
    g18: LineSegment StartX=-6.5 StartY=55.88 StartZ=0 EndX=-6.5 EndY=50.8 EndZ=0
    g19: LineSegment StartX=-6.5 StartY=50.8 StartZ=0 EndX=-7.5 EndY=50.8 EndZ=0
    g20: LineSegment StartX=-7.5 StartY=50.8 StartZ=0 EndX=-7.5 EndY=45.72 EndZ=0
    g21: LineSegment StartX=-7.5 StartY=45.72 StartZ=0 EndX=-8.5 EndY=45.72 EndZ=0
    g22: LineSegment StartX=-8.5 StartY=45.72 StartZ=0 EndX=-8.5 EndY=40.64 EndZ=0
    g23: LineSegment StartX=-8.5 StartY=40.64 StartZ=0 EndX=-9.5 EndY=40.64 EndZ=0
    g24: LineSegment StartX=-9.5 StartY=40.64 StartZ=0 EndX=-9.5 EndY=35.56 EndZ=0
    g25: LineSegment StartX=-9.5 StartY=35.56 StartZ=0 EndX=-10.5 EndY=35.56 EndZ=0
    g26: LineSegment StartX=-10.5 StartY=35.56 StartZ=0 EndX=-10.5 EndY=30.48 EndZ=0
    g27: LineSegment StartX=-10.5 StartY=30.48 StartZ=0 EndX=-11.5 EndY=30.48 EndZ=0
    g28: LineSegment StartX=-11.5 StartY=30.48 StartZ=0 EndX=-11.5 EndY=25.4 EndZ=0
    g29: LineSegment StartX=-11.5 StartY=25.4 StartZ=0 EndX=-12.5 EndY=25.4 EndZ=0
    g30: LineSegment StartX=-12.5 StartY=25.4 StartZ=0 EndX=-12.5 EndY=20.32 EndZ=0
    g31: LineSegment StartX=-12.5 StartY=20.32 StartZ=0 EndX=-13.5 EndY=20.32 EndZ=0
    g32: LineSegment StartX=-13.5 StartY=20.32 StartZ=0 EndX=-13.5 EndY=15.24 EndZ=0
    g33: LineSegment StartX=-13.5 StartY=15.24 StartZ=0 EndX=-14.5 EndY=15.24 EndZ=0
    g34: LineSegment StartX=-14.5 StartY=15.24 StartZ=0 EndX=-14.5 EndY=10.16 EndZ=0
    g35: LineSegment StartX=-14.5 StartY=10.16 StartZ=0 EndX=-15.5 EndY=10.16 EndZ=0
    g36: LineSegment StartX=-15.5 StartY=10.16 StartZ=0 EndX=-15.5 EndY=5.08 EndZ=0
    g37: LineSegment StartX=-15.5 StartY=5.08 StartZ=0 EndX=-16.5 EndY=5.08 EndZ=0
    g38: LineSegment StartX=-16.5 StartY=5.08 StartZ=0 EndX=-16.5 EndY=0 EndZ=0
    g39: LineSegment StartX=2.5 StartY=101.6 StartZ=0 EndX=7 EndY=101.6 EndZ=0
    g40: LineSegment StartX=7 StartY=101.6 StartZ=0 EndX=7 EndY=0 EndZ=0
    g41: LineSegment StartX=7 StartY=0 StartZ=0 EndX=-16.5 EndY=0 EndZ=0
  constraints (126):
    c: Vertical(g0)
    c: Horizontal(g1)
    c: Coincident(g1,g0)
    c: DistanceX(g1,g0) = 1
    c: Coincident(g2,g1)
    c: Vertical(g2)
    c: Coincident(g3,g2)
    c: Horizontal(g3)
    c: Coincident(g4,g3)
    c: Vertical(g4)
    c: Coincident(g5,g4)
    c: Horizontal(g5)
    c: Coincident(g6,g5)
    c: Vertical(g6)
    c: Coincident(g7,g6)
    c: Horizontal(g7)
    c: Coincident(g8,g7)
    c: Vertical(g8)
    c: Coincident(g9,g8)
    c: Horizontal(g9)
    c: Coincident(g10,g9)
    c: Vertical(g10)
    c: Coincident(g11,g10)
    c: Horizontal(g11)
    c: Coincident(g12,g11)
    c: Vertical(g12)
    c: Coincident(g13,g12)
    c: Horizontal(g13)
    c: Equal(g0,g2)
    c: Equal(g1,g3)
    c: Equal(g3,g5)
    c: Equal(g5,g7)
    c: Equal(g7,g9)
    c: Equal(g9,g11)
    c: Equal(g11,g13)
    c: Equal(g2,g4)
    c: Equal(g4,g6)
    c: Equal(g6,g8)
    c: Equal(g8,g10)
    c: Equal(g10,g12)
    c: DistanceY(g-1,g0) = 101.6
    c: Coincident(g14,g13)
    c: Vertical(g14)
    c: Coincident(g15,g14)
    c: Horizontal(g15)
    c: Coincident(g16,g15)
    c: Vertical(g16)
    c: Coincident(g17,g16)
    c: Horizontal(g17)
    c: Coincident(g18,g17)
    c: Vertical(g18)
    c: Coincident(g19,g18)
    c: Horizontal(g19)
    c: Coincident(g20,g19)
    c: Vertical(g20)
    c: Coincident(g21,g20)
    c: Horizontal(g21)
    c: Coincident(g22,g21)
    c: Vertical(g22)
    c: Coincident(g23,g22)
    c: Horizontal(g23)
    c: Coincident(g24,g23)
    c: Vertical(g24)
    c: Coincident(g25,g24)
    c: Horizontal(g25)
    c: Coincident(g26,g25)
    c: Vertical(g26)
    c: Coincident(g27,g26)
    c: Horizontal(g27)
    c: Coincident(g28,g27)
    c: Vertical(g28)
    c: Coincident(g29,g28)
    c: Horizontal(g29)
    c: Coincident(g30,g29)
    c: Vertical(g30)
    c: Coincident(g31,g30)
    c: Horizontal(g31)
    c: Coincident(g32,g31)
    c: Vertical(g32)
    c: Coincident(g33,g32)
    c: Horizontal(g33)
    c: Coincident(g34,g33)
    c: Vertical(g34)
    c: Coincident(g35,g34)
    c: Horizontal(g35)
    c: Coincident(g36,g35)
    c: Vertical(g36)
    c: Coincident(g37,g36)
    c: Horizontal(g37)
    c: Coincident(g38,g37)
    c: PointOnObject(g38,g-1)
    c: Vertical(g38)
    c: Equal(g13,g15)
    c: Equal(g12,g14)
    c: Equal(g14,g16)
    c: Equal(g15,g17)
    c: Equal(g17,g19)
    c: Equal(g16,g18)
    c: Equal(g18,g20)
    c: Equal(g19,g21)
    c: Equal(g21,g23)
    c: Equal(g20,g22)
    c: Equal(g22,g24)
    c: Equal(g23,g25)
    c: Equal(g25,g27)
    c: Equal(g24,g26)
    c: Equal(g26,g28)
    c: Equal(g27,g29)
    c: Equal(g29,g31)
    c: Equal(g28,g30)
    c: Equal(g30,g32)
    c: Equal(g31,g33)
    c: Equal(g33,g35)
    c: Equal(g32,g34)
    c: Equal(g34,g36)
    c: Equal(g35,g37)
    c: Equal(g36,g38)
    c: Coincident(g39,g0)
    c: Horizontal(g39)
    c: Coincident(g40,g39)
    c: PointOnObject(g40,g-1)
    c: Vertical(g40)
    c: Coincident(g41,g40)
    c: Coincident(g41,g38)
    c: DistanceX(g-1,g40) = 7
    c: DistanceX(g-1,g0) = 2.5
FEATURE [PartDesign::Pocket] Pocket001
  AddSubType = 1
  AutoTaperInnerAngle = true
  BaseFeature = -> Pad003
  CheckUpToFaceLimits = true
  ClaimChildren = false
  Fit = 0
  FitJoin = 0
  InnerFit = 0
  InnerFitJoin = 0
  InvalidShape = false
  Length = 3
  Length2 = 3
  Linearize = true
  NewSolid = false
  Profile = -> Sketch009
  Suppress = false
  TaperInnerAngle = 0
  TaperInnerAngleRev = 0
  TreeRank = 41
  Type = 4
  ValidateShape = true
  _ProfileBasedVersion = 1
  _Version = 1
FEATURE [Sketcher::SketchObject] Sketch010
  ArcFitTolerance = 1e-06
  AttachmentSupport = -> [Pocket001]
  ExternalBSplineMaxDegree = 5
  ExternalBSplineTolerance = 0.0001
  FullyConstrained = true
  InternalTolerance = 1e-06
  InvalidShape = false
  MakeInternals = false
  MapMode = 5
  Placement = pos=(1.6e-15,7,-1.6e-15) rot=(0,0.707107,0.707107;3.14159rad)
  Support = -> [Pocket001]
  TreeRank = 42
  ValidateShape = true
  expr: Constraints[2] = <<Parameters>>.height / 40
  sketch-geometry (1):
    g0: Circle CenterX=0 CenterY=2.54 CenterZ=0 NormalX=0 NormalY=0 NormalZ=1 AngleXU=0 Radius=1.625
  constraints (3):
    c: PointOnObject(g0,g-2)
    c: Diameter(g0) = 3.25
    c: DistanceY(g-1,g0) = 2.54
FEATURE [PartDesign::Pocket] Pocket002
  AddSubType = 1
  AutoTaperInnerAngle = true
  BaseFeature = -> Pocket001
  CheckUpToFaceLimits = true
  ClaimChildren = false
  Fit = 0
  FitJoin = 0
  InnerFit = 0
  InnerFitJoin = 0
  InvalidShape = false
  Length = 500
  Length2 = 500
  Linearize = true
  NewSolid = false
  Profile = -> Sketch010
  Suppress = false
  TaperInnerAngle = 0
  TaperInnerAngleRev = 0
  TreeRank = 43
  Type = 4
  ValidateShape = true
  _ProfileBasedVersion = 1
  _Version = 1
FEATURE [PartDesign::LinearPattern] LinearPattern
  AddSubType = 0
  BaseFeature = -> Pocket002
  CopyShape = false
  Direction = -> Z_Axis001
  InvalidShape = false
  Length = 101.6
  NewSolid = false
  Occurrences = 21
  ParallelTransform = true
  SubTransform = true
  Suppress = false
  TreeRank = 44
  ValidateShape = true
  _Version = 3
  expr: Length = <<Parameters>>.height
FEATURE [PartDesign::Body] Body001  label="Height Adjustment"
  AutoGroupSolids = false
  ClaimAllChildren = false
  ExportMode = 0
  Group = -> [Sketch007,Pad002,Sketch008,Pad003,Sketch009,Pocket001,Sketch010,Pocket002,LinearPattern]
  InvalidShape = false
  Origin = -> Origin001
  Tip = -> LinearPattern
  TreeRank = 35
  ValidateShape = true
  _ExportChildren = -> [Pad002,Pad003,Pocket001,Pocket002,LinearPattern]
  _GroupVersion = 1
FEATURE [Sketcher::SketchObject] Sketch011
  ArcFitTolerance = 1e-06
  AttachmentSupport = -> [XZ_Plane002]
  ExternalBSplineMaxDegree = 5
  ExternalBSplineTolerance = 0.0001
  FullyConstrained = true
  InternalTolerance = 1e-06
  InvalidShape = false
  MakeInternals = false
  MapMode = 5
  Placement = pos=(0,0,0) rot=(1,0,0;1.5708rad)
  Support = -> [XZ_Plane002]
  TreeRank = 55
  ValidateShape = true
  expr: Constraints[2] = <<Parameters>>.outer_diameter
  expr: Constraints[3] = <<Parameters>>.outer_diameter + 2 * <<Parameters>>.thickness
  sketch-geometry (2):
    g0: Circle CenterX=0 CenterY=0 CenterZ=0 NormalX=0 NormalY=0 NormalZ=1 AngleXU=0 Radius=45
    g1: Circle CenterX=0 CenterY=0 CenterZ=0 NormalX=0 NormalY=0 NormalZ=1 AngleXU=0 Radius=47.5
  constraints (4):
    c: Coincident(g0,g-1)
    c: Coincident(g1,g0)
    c: Diameter(g0) = 90
    c: Diameter(g1) = 95
FEATURE [PartDesign::Pad] Pad004
  AddSubType = 0
  AlongSketchNormal = false
  AutoTaperInnerAngle = true
  CheckUpToFaceLimits = true
  ClaimChildren = false
  Direction = (0,-1,2e-16)
  Fit = 0
  FitJoin = 0
  InnerFit = 0
  InnerFitJoin = 0
  InvalidShape = false
  Length = 32.4
  Length2 = 100
  Linearize = true
  NewSolid = false
  Profile = -> Sketch011
  Suppress = false
  TaperInnerAngle = 0
  TaperInnerAngleRev = 0
  TreeRank = 56
  Type = 0
  ValidateShape = true
  _ProfileBasedVersion = 1
  expr: Length = <<Parameters>>.height / <<Parameters>>.thread_turns + <<Parameters>>.thread_large_width
FEATURE [Sketcher::SketchObject] Sketch012
  ArcFitTolerance = 1e-06
  AttachmentSupport = -> [XY_Plane002]
  ExternalBSplineMaxDegree = 5
  ExternalBSplineTolerance = 0.0001
  FullyConstrained = true
  InternalTolerance = 1e-06
  InvalidShape = false
  MakeInternals = false
  MapMode = 5
  Support = -> [XY_Plane002]
  TreeRank = 57
  ValidateShape = true
  expr: Constraints[11] = <<Parameters>>.outer_diameter / 2
  expr: Constraints[7] = <<Parameters>>.thread_large_width
  expr: Constraints[8] = <<Parameters>>.thread_small_width
  expr: Constraints[9] = <<Parameters>>.thread_depth
  sketch-geometry (4):
    g0: LineSegment StartX=-45 StartY=-7 StartZ=0 EndX=-45 EndY=0 EndZ=0
    g1: LineSegment StartX=-42.7 StartY=-1.75 StartZ=0 EndX=-42.7 EndY=-5.25 EndZ=0
    g2: LineSegment StartX=-42.7 StartY=-1.75 StartZ=0 EndX=-45 EndY=0 EndZ=0
    g3: LineSegment StartX=-42.7 StartY=-5.25 StartZ=0 EndX=-45 EndY=-7 EndZ=0
  constraints (12):
    c: Vertical(g0)
    c: Vertical(g1)
    c: Coincident(g2,g1)
    c: Coincident(g2,g0)
    c: Coincident(g3,g1)
    c: Coincident(g3,g0)
    c: Equal(g2,g3)
    c: DistanceY(g0,g0) = 7
    c: DistanceY(g1,g1) = 3.5
    c: DistanceX(g0,g1) = 2.3
    c: PointOnObject(g0,g-1)
    c: DistanceX(g0,g-1) = 45
FEATURE [PartDesign::AdditiveHelix] Helix001
  AddSubType = 0
  Angle = 0
  Axis = (0,1,0)
  Base = (0,0,0)
  BaseFeature = -> Pad004
  ClaimChildren = false
  Fit = 0
  FitJoin = 0
  Growth = 0
  HasBeenEdited = true
  Height = 25.4
  InnerFit = 0
  InnerFitJoin = 0
  InvalidShape = false
  LeftHanded = false
  Linearize = true
  Mode = 0
  NewSolid = false
  Outside = false
  Pitch = 25.4
  Profile = -> Sketch012
  ReferenceAxis = -> Sketch012 [V_Axis]
  Reversed = true
  Suppress = false
  TreeRank = 58
  Turns = 1
  ValidateShape = true
  _ProfileBasedVersion = 1
  expr: Height = <<Parameters>>.height / <<Parameters>>.thread_turns
  expr: Pitch = <<Parameters>>.thread_pitch
FEATURE [PartDesign::Body] Body002  label="Test"
  AutoGroupSolids = false
  ClaimAllChildren = false
  ExportMode = 0
  Group = -> [Sketch011,Pad004,Sketch012,Helix001]
  InvalidShape = false
  Origin = -> Origin002
  Tip = -> Helix001
  TreeRank = 54
  ValidateShape = true
  _ExportChildren = -> [Pad004,Helix001]
  _GroupVersion = 1
